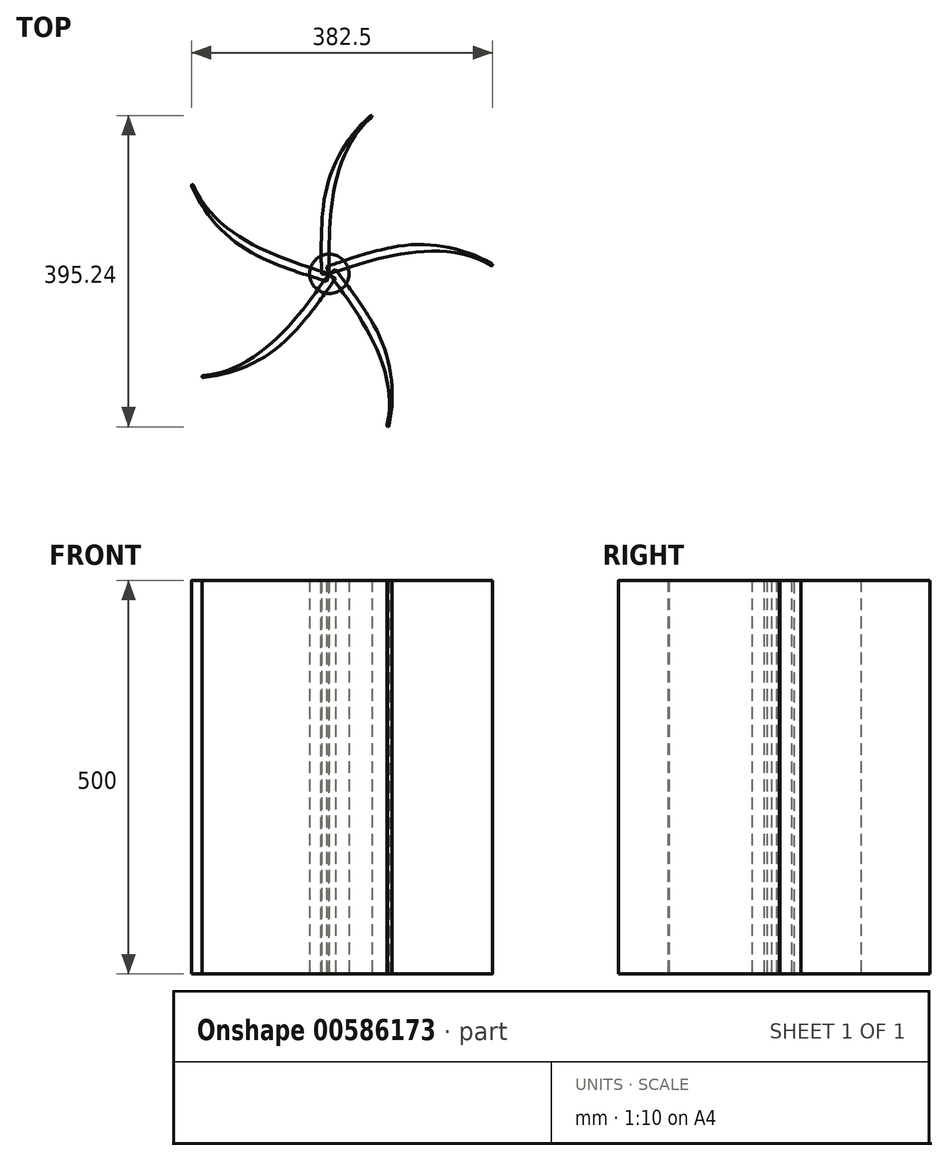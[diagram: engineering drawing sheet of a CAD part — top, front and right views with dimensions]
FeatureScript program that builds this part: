
annotation { "Feature Type Name" : "Feature", "Feature Type Description" : "" }
export const myFeature = defineFeature(function(context is Context, id is Id, definition is map)
    precondition{}
    {
        {
            var Q0;
            Q0=qCreatedBy(makeId("Top.planeOp"),FACE);
            var sketch = newSketch(context, id + "F0", { "sketchPlane" : qUnion([Q0])});
            skCircle(sketch, "E0", {"center": v(0, 0) * mm, "radius": 25 * mm});
            skSolve(sketch);
        }
        {
            var Q0;
            Q0=makeQuery(id+"F0.imprint","IMPRINT",FACE,{"disambiguationData":[TD([[makeQuery(id+"F0.imprint","IMPRINT",EDGE,{"derivedFrom":sQuery(id+"F0.wireOp",EDGE,"E0")}),1.0]])]});
            extrude(context, id + "F1", {"entities" : qUnion([Q0]), "endBound" : BoundingType.SYMMETRIC, "depth" : 500 * mm, "offsetDistance" : 25 * mm});
        }
        {
            var Q0;
            Q0=qCreatedBy(makeId("Top.planeOp"),FACE);
            var sketch = newSketch(context, id + "F2", { "sketchPlane" : qUnion([Q0])});
            skFitSpline(sketch, "E1", {"points": [v(55, 200) * mm, v(0, 0) * mm], "startDerivative": vector(-180, -150) * mm, "endDerivative": vector(0, -150) * mm});
            skFitSpline(sketch, "E2.0", {"points": [v(48.6, 207.68) * mm, v(44.52, 204.28) * mm, v(36.92, 197.06) * mm, v(27.1, 185.17) * mm, v(18.78, 172.42) * mm, v(9.5, 154.5) * mm, v(0.97, 130.83) * mm, v(-5.36, 101.6) * mm, v(-8.73, 72.66) * mm, v(-10.04, 45.15) * mm, v(-10.14, 24.39) * mm, v(-10.04, 9.69) * mm, v(-10, 3.08) * mm, v(-10, 0) * mm]});
            skLineSegment(sketch, "E3", {"start": v(-10, 0) * mm, "end": v(0, 0) * mm});
            skLineSegment(sketch, "E4", {"start": v(48.6, 207.68) * mm, "end": v(55, 200) * mm});
            skSolve(sketch);
        }
        {
            var Q0;
            Q0 = qSketchRegion(id + "F2", true);
            extrude(context, id + "F3", {"entities" : qUnion([Q0]), "endBound" : BoundingType.SYMMETRIC, "depth" : 500 * mm, "offsetDistance" : 25 * mm});
        }
        {
            var Q0;
            Q0=makeQuery(id+"F3.opExtrude","SWEPT_EDGE",EDGE,{"disambiguationData":[OSD([sQuery(id+"F2.wireOp",EDGE,"E2.0"),sQuery(id+"F2.wireOp",EDGE,"E4")])]});
            chamfer(context, id + "F4", {"entities" : qUnion([Q0]), "chamferType" : ChamferType.TWO_OFFSETS, "width1" : 25 * mm, "oppositeDirection" : false, "width2" : 5 * mm, "tangentPropagation" : true});
        }
        {
            var Q0;
            {var subQ0=sQuery(id+"F2.wireOp",EDGE,"E2.0");Q0=makeQuery(id+"F4.opChamfer","BLEND_EDGE",EDGE,{"blendedFrom":[makeQuery(id+"F3.opExtrude","SWEPT_EDGE",EDGE,{"disambiguationData":[OSD([subQ0,sQuery(id+"F2.wireOp",EDGE,"E4")])]}),makeQuery(id+"F3.opExtrude","SWEPT_FACE",FACE,{"disambiguationData":[OSD([subQ0])]})],"blendedInto":[makeQuery(id+"F3.opExtrude","SWEPT_FACE",FACE,{"disambiguationData":[OSD([subQ0])]})]});}
            fillet(context, id + "F5", {"entities" : qUnion([Q0]), "radius" : 180 * mm, "tangentPropagation" : true, "allowEdgeOverflow" : false});
        }
        {
            var Q0;
            Q0=makeQuery(id+"F3.opExtrude","SWEPT_EDGE",EDGE,{"disambiguationData":[OSD([sQuery(id+"F2.wireOp",EDGE,"E1"),sQuery(id+"F2.wireOp",EDGE,"E4")])]});
            var Q1;
            {var subQ0=sQuery(id+"F2.wireOp",EDGE,"E4");var subQ1=sQuery(id+"F2.wireOp",EDGE,"E2.0");Q1=makeQuery(id+"F5.opFillet","BLEND_EDGE",EDGE,{"blendedFrom":[makeQuery(id+"F4.opChamfer","BLEND_EDGE",EDGE,{"blendedFrom":[makeQuery(id+"F3.opExtrude","SWEPT_EDGE",EDGE,{"disambiguationData":[OSD([subQ1,subQ0])]}),makeQuery(id+"F3.opExtrude","SWEPT_FACE",FACE,{"disambiguationData":[OSD([subQ1])]})],"blendedInto":[makeQuery(id+"F3.opExtrude","SWEPT_FACE",FACE,{"disambiguationData":[OSD([subQ1])]})]}),makeQuery(id+"F3.opExtrude","SWEPT_FACE",FACE,{"disambiguationData":[OSD([subQ0])]})],"blendedInto":[makeQuery(id+"F3.opExtrude","SWEPT_FACE",FACE,{"disambiguationData":[OSD([subQ0])]})]});}
            fillet(context, id + "F6", {"entities" : qUnion([Q0, Q1]), "radius" : 2 * mm, "tangentPropagation" : true, "allowEdgeOverflow" : false});
        }
        {
            var Q0;
            Q0=makeQuery(id+"F3.opExtrude","SWEPT_BODY",BODY,{"disambiguationData":[OSD([sQuery(id+"F2.wireOp",EDGE,"E1"),sQuery(id+"F2.wireOp",EDGE,"E2.0"),sQuery(id+"F2.wireOp",EDGE,"E3"),sQuery(id+"F2.wireOp",EDGE,"E4")])]});
            var Q1;
            Q1=makeQuery(id+"F1.opExtrude","SWEPT_FACE",FACE,{"disambiguationData":[OSD([sQuery(id+"F0.wireOp",EDGE,"E0")])]});
            circularPattern(context, id + "F7", {"entities" : qUnion([Q0]), "axis" : qUnion([Q1]), "angle" : 360 * degree, "instanceCount" : 5, "equalSpace" : true});
        }
    });
